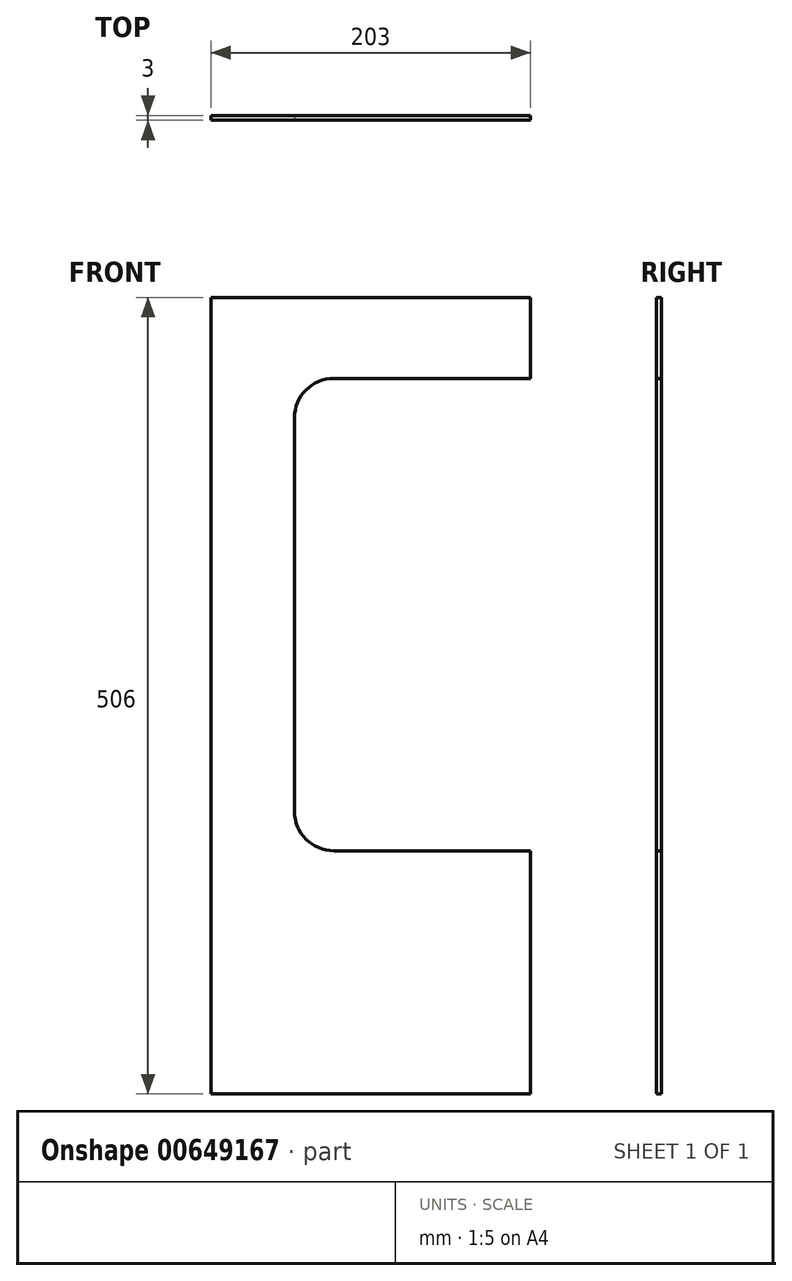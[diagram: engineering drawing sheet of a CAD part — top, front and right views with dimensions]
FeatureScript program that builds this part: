
annotation { "Feature Type Name" : "Feature", "Feature Type Description" : "" }
export const myFeature = defineFeature(function(context is Context, id is Id, definition is map)
    precondition{}
    {
        {
            var Q0;
            Q0=qCreatedBy(makeId("Front.planeOp"),FACE);
            var sketch = newSketch(context, id + "F0", { "sketchPlane" : qUnion([Q0])});
            skLineSegment(sketch, "E0.bottom", {"start": v(101.5, 201.5) * mm, "end": v(-101.5, 201.5) * mm});
            skLineSegment(sketch, "E0.top", {"start": v(101.5, -201.5) * mm, "end": v(-101.5, -201.5) * mm});
            skLineSegment(sketch, "E0.left", {"start": v(101.5, 201.5) * mm, "end": v(101.5, -201.5) * mm});
            skLineSegment(sketch, "E0.right", {"start": v(-101.5, 201.5) * mm, "end": v(-101.5, -201.5) * mm});
            skPoint(sketch, "E0.middle", {"position": v(0, 0) * mm});
            skSolve(sketch);
        }
        {
            var Q0;
            Q0=makeQuery(id+"F0.imprint","IMPRINT",FACE,{"disambiguationData":[TD([[makeQuery(id+"F0.imprint","IMPRINT",EDGE,{"derivedFrom":sQuery(id+"F0.wireOp",EDGE,"E0.bottom")}),1.0]])]});
            extrude(context, id + "F1", {"entities" : qUnion([Q0]), "depth" : 3 * mm, "offsetDistance" : 25 * mm});
        }
        {
            var Q0;
            Q0=makeQuery(id+"F1.opExtrude","CAP_FACE",FACE,{"disambiguationData":[OSD([sQuery(id+"F0.wireOp",EDGE,"E0.bottom"),sQuery(id+"F0.wireOp",EDGE,"E0.top"),sQuery(id+"F0.wireOp",EDGE,"E0.left"),sQuery(id+"F0.wireOp",EDGE,"E0.right")])],"isStart":false});
            var sketch = newSketch(context, id + "F2", { "sketchPlane" : qUnion([Q0])});
            skLineSegment(sketch, "E1", {"start": v(101.5, 0) * mm, "end": v(-48.5, 0) * mm, "construction": true});
            skLineSegment(sketch, "E2", {"start": v(-48.5, 0) * mm, "end": v(-48.5, 150) * mm, "construction": true});
            skLineSegment(sketch, "E3", {"start": v(101.5, 0) * mm, "end": v(101.5, -150) * mm, "construction": true});
            skLineSegment(sketch, "E4.bottom", {"start": v(-48.5, 150) * mm, "end": v(101.5, 150) * mm});
            skLineSegment(sketch, "E4.top", {"start": v(-48.5, -150) * mm, "end": v(101.5, -150) * mm});
            skLineSegment(sketch, "E4.left", {"start": v(-48.5, 150) * mm, "end": v(-48.5, -150) * mm});
            skLineSegment(sketch, "E4.right", {"start": v(101.5, 150) * mm, "end": v(101.5, -150) * mm});
            skSolve(sketch);
        }
        {
            var Q0;
            Q0 = qSketchRegion(id + "F2", true);
            extrude(context, id + "F3", {"entities" : qUnion([Q0]), "operationType" : NewBodyOperationType.REMOVE, "oppositeDirection" : true, "depth" : 25 * mm, "offsetDistance" : 25 * mm});
        }
        {
            var Q0;
            Q0=makeQuery(id+"F3.boolean.opBoolean","COPY",EDGE,{"derivedFrom":makeQuery(id+"F3.opExtrude","SWEPT_EDGE",EDGE,{"disambiguationData":[OSD([sQuery(id+"F2.wireOp",EDGE,"E4.bottom"),sQuery(id+"F2.wireOp",EDGE,"E4.left")])]})});
            var Q1;
            Q1=makeQuery(id+"F3.boolean.opBoolean","COPY",EDGE,{"derivedFrom":makeQuery(id+"F3.opExtrude","SWEPT_EDGE",EDGE,{"disambiguationData":[OSD([sQuery(id+"F2.wireOp",EDGE,"E4.top"),sQuery(id+"F2.wireOp",EDGE,"E4.left")])]})});
            fillet(context, id + "F4", {"entities" : qUnion([Q0, Q1]), "radius" : 25 * mm, "tangentPropagation" : true, "allowEdgeOverflow" : false});
        }
        {
            var Q0;
            Q0=makeQuery(id+"F1.opExtrude","CAP_FACE",FACE,{"disambiguationData":[OSD([sQuery(id+"F0.wireOp",EDGE,"E0.bottom"),sQuery(id+"F0.wireOp",EDGE,"E0.top"),sQuery(id+"F0.wireOp",EDGE,"E0.left"),sQuery(id+"F0.wireOp",EDGE,"E0.right")])],"isStart":false});
            var sketch = newSketch(context, id + "F5", { "sketchPlane" : qUnion([Q0])});
            skLineSegment(sketch, "E5", {"start": v(-101.5, 201.5) * mm, "end": v(-101.5, -304.5) * mm, "construction": true});
            skLineSegment(sketch, "E6.bottom", {"start": v(-101.5, -304.5) * mm, "end": v(101.5, -304.5) * mm});
            skLineSegment(sketch, "E6.top", {"start": v(-101.5, -201.5) * mm, "end": v(101.5, -201.5) * mm});
            skLineSegment(sketch, "E6.left", {"start": v(-101.5, -304.5) * mm, "end": v(-101.5, -201.5) * mm});
            skLineSegment(sketch, "E6.right", {"start": v(101.5, -304.5) * mm, "end": v(101.5, -201.5) * mm});
            skSolve(sketch);
        }
        {
            var Q0;
            Q0 = qSketchRegion(id + "F5", true);
            var Q1;
            Q1=makeQuery(id+"F1.opExtrude","CAP_FACE",FACE,{"disambiguationData":[OSD([sQuery(id+"F0.wireOp",EDGE,"E0.bottom"),sQuery(id+"F0.wireOp",EDGE,"E0.top"),sQuery(id+"F0.wireOp",EDGE,"E0.left"),sQuery(id+"F0.wireOp",EDGE,"E0.right")])],"isStart":true});
            extrude(context, id + "F6", {"entities" : qUnion([Q0]), "operationType" : NewBodyOperationType.ADD, "endBound" : BoundingType.UP_TO_SURFACE, "oppositeDirection" : true, "depth" : 25 * mm, "endBoundEntityFace" : qUnion([Q1]), "offsetDistance" : 25 * mm});
        }
    });
